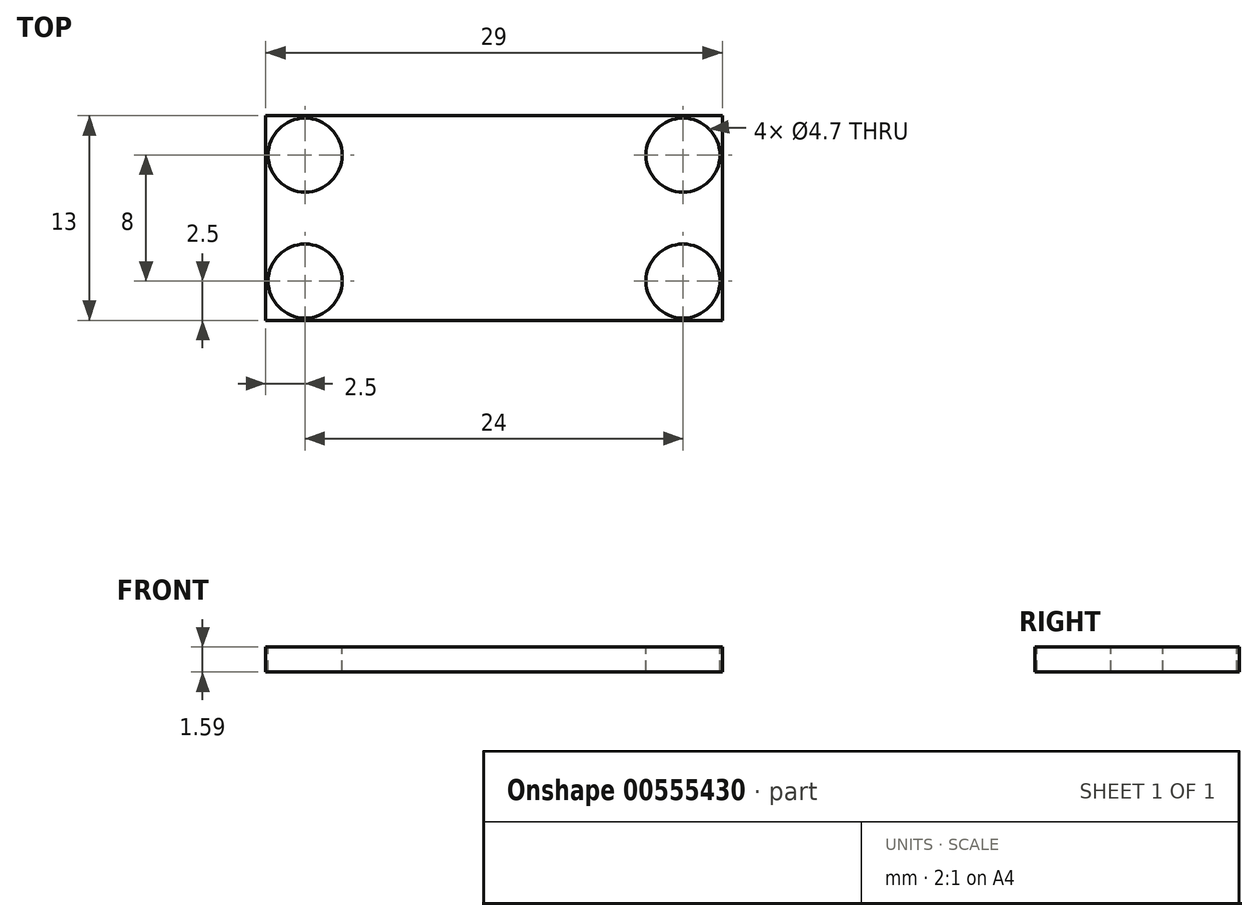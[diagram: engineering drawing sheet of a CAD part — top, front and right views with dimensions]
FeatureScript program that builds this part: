
annotation { "Feature Type Name" : "Feature", "Feature Type Description" : "" }
export const myFeature = defineFeature(function(context is Context, id is Id, definition is map)
    precondition{}
    {
        {
            var Q0;
            Q0=qCreatedBy(makeId("Top.planeOp"),FACE);
            var sketch = newSketch(context, id + "F0", { "sketchPlane" : qUnion([Q0])});
            skLineSegment(sketch, "E0.bottom", {"start": v(-14.5, 6.5) * mm, "end": v(14.5, 6.5) * mm});
            skLineSegment(sketch, "E0.top", {"start": v(-14.5, -6.5) * mm, "end": v(14.5, -6.5) * mm});
            skLineSegment(sketch, "E0.left", {"start": v(-14.5, 6.5) * mm, "end": v(-14.5, -6.5) * mm});
            skLineSegment(sketch, "E0.right", {"start": v(14.5, 6.5) * mm, "end": v(14.5, -6.5) * mm});
            skPoint(sketch, "E0.middle", {"position": v(0, 0) * mm});
            skSolve(sketch);
        }
        {
            var Q0;
            Q0 = qSketchRegion(id + "F0", true);
            extrude(context, id + "F1", {"entities" : qUnion([Q0]), "depth" : 1.59 * mm, "offsetDistance" : 25.4 * mm});
        }
        {
            var Q0;
            Q0=qCreatedBy(makeId("Top.planeOp"),FACE);
            var sketch = newSketch(context, id + "F2", { "sketchPlane" : qUnion([Q0])});
            skCircle(sketch, "E1", {"center": v(-62.36, 0) * mm, "radius": 6.25 * mm});
            skSolve(sketch);
        }
        {
            var Q0;
            Q0 = qSketchRegion(id + "F2", true);
            extrude(context, id + "F3", {"entities" : qUnion([Q0]), "depth" : 2 * mm, "offsetDistance" : 25.4 * mm});
        }
        {
            var Q0;
            Q0=makeQuery(id+"F3.opExtrude","SWEPT_BODY",BODY,{"disambiguationData":[OSD([sQuery(id+"F2.wireOp",EDGE,"E1")])]});
            deleteBodies(context, id + "F4", {"entities" : qUnion([Q0])});
        }
        {
            var Q0;
            Q0=makeQuery(id+"F1.opExtrude","CAP_FACE",FACE,{"disambiguationData":[OSD([sQuery(id+"F0.wireOp",EDGE,"E0.bottom"),sQuery(id+"F0.wireOp",EDGE,"E0.top"),sQuery(id+"F0.wireOp",EDGE,"E0.left"),sQuery(id+"F0.wireOp",EDGE,"E0.right")])],"isStart":false});
            var sketch = newSketch(context, id + "F5", { "sketchPlane" : qUnion([Q0])});
            skLineSegment(sketch, "E2", {"start": v(-14.5, 0) * mm, "end": v(14.5, 0) * mm, "construction": true});
            skLineSegment(sketch, "E3", {"start": v(0, -6.5) * mm, "end": v(0, 6.5) * mm, "construction": true});
            skCircle(sketch, "E4", {"center": v(-12, 4) * mm, "radius": 2.35 * mm});
            skCircle(sketch, "E5.MirrorC", {"center": v(-12, -4) * mm, "radius": 2.35 * mm});
            skCircle(sketch, "E6.MirrorC", {"center": v(12, -4) * mm, "radius": 2.35 * mm});
            skCircle(sketch, "E7.MirrorC", {"center": v(12, 4) * mm, "radius": 2.35 * mm});
            skSolve(sketch);
        }
        {
            var Q0;
            Q0 = qSketchRegion(id + "F5", true);
            extrude(context, id + "F6", {"entities" : qUnion([Q0]), "operationType" : NewBodyOperationType.REMOVE, "oppositeDirection" : true, "depth" : 25.4 * mm, "offsetDistance" : 25.4 * mm});
        }
    });
